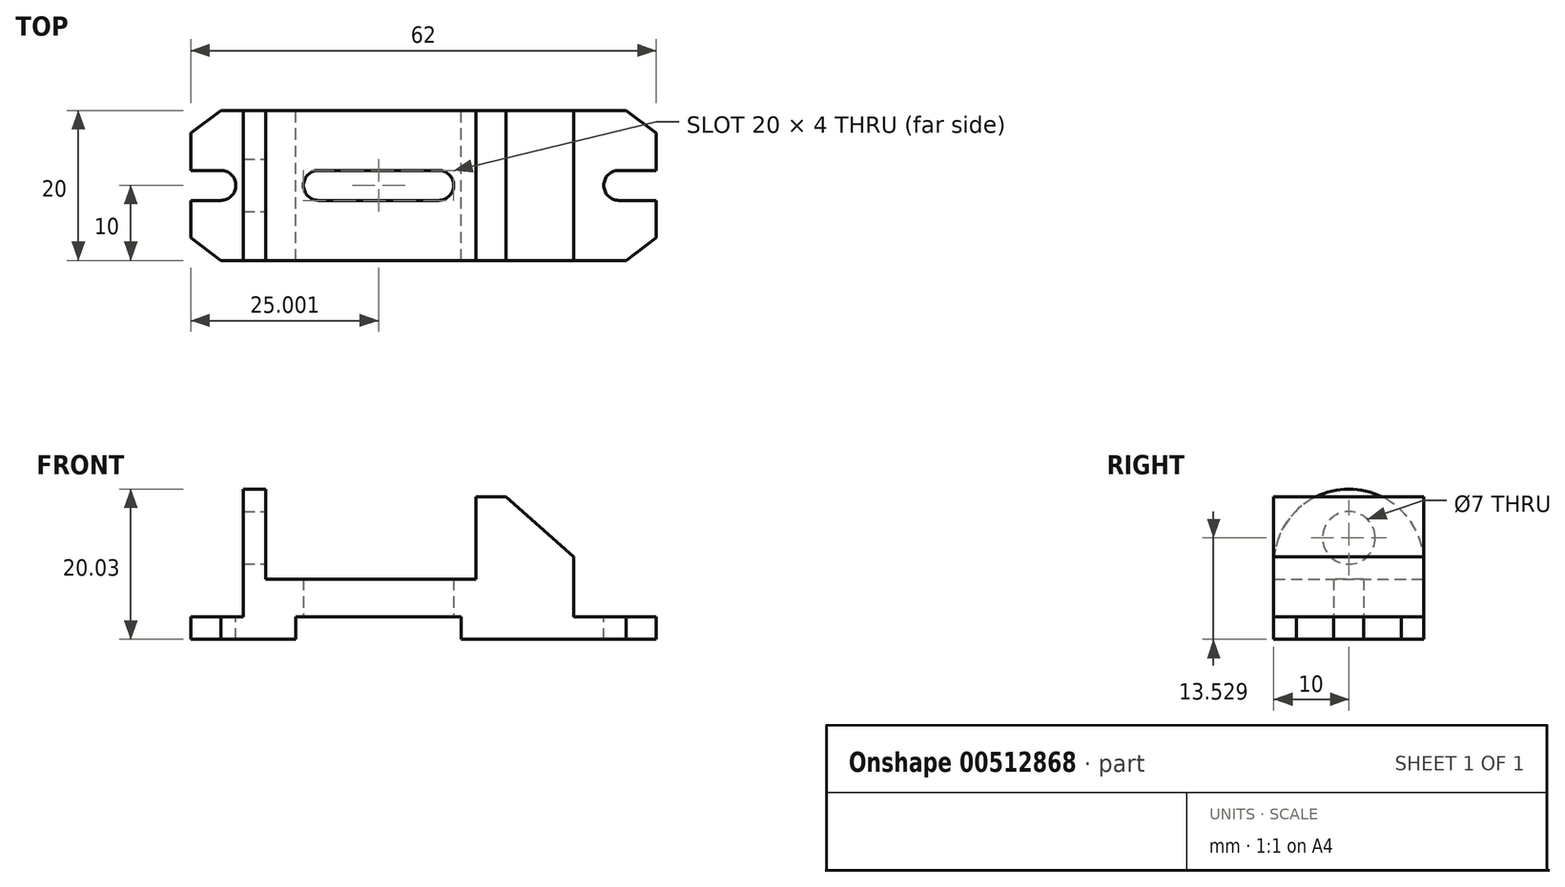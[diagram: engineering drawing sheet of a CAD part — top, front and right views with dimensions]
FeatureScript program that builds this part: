
annotation { "Feature Type Name" : "Feature", "Feature Type Description" : "" }
export const myFeature = defineFeature(function(context is Context, id is Id, definition is map)
    precondition{}
    {
        {
            var Q0;
            Q0=qCreatedBy(makeId("Front.planeOp"),FACE);
            var sketch = newSketch(context, id + "F0", { "sketchPlane" : qUnion([Q0])});
            skLineSegment(sketch, "E0", {"start": v(-17.84, 0) * mm, "end": v(-17.84, 3) * mm});
            skLineSegment(sketch, "E1", {"start": v(-17.84, 3) * mm, "end": v(-14.84, 3) * mm});
            skLineSegment(sketch, "E2", {"start": v(-14.84, 3) * mm, "end": v(-14.84, 10.03) * mm});
            skLineSegment(sketch, "E3", {"start": v(-14.84, 10.03) * mm, "end": v(-11.84, 10.03) * mm});
            skLineSegment(sketch, "E4", {"start": v(-11.84, 10.03) * mm, "end": v(-11.84, 8.03) * mm});
            skLineSegment(sketch, "E5", {"start": v(-11.84, 8.03) * mm, "end": v(16.16, 8.03) * mm});
            skLineSegment(sketch, "E6", {"start": v(16.16, 8.03) * mm, "end": v(16.16, 19.03) * mm});
            skLineSegment(sketch, "E7", {"start": v(16.16, 19.03) * mm, "end": v(20.16, 19.03) * mm});
            skLineSegment(sketch, "E8", {"start": v(-17.84, 0) * mm, "end": v(-7.84, 0) * mm});
            skLineSegment(sketch, "E9", {"start": v(-7.84, 0) * mm, "end": v(-7.84, 3) * mm});
            skLineSegment(sketch, "E10", {"start": v(-7.84, 3) * mm, "end": v(14.16, 3) * mm});
            skLineSegment(sketch, "E11", {"start": v(14.16, 3) * mm, "end": v(14.16, 0) * mm});
            skLineSegment(sketch, "E12", {"start": v(14.16, 0) * mm, "end": v(36.16, 0) * mm});
            skLineSegment(sketch, "E13", {"start": v(36.16, 0) * mm, "end": v(36.16, 3) * mm});
            skLineSegment(sketch, "E14", {"start": v(36.16, 3) * mm, "end": v(29.16, 3) * mm});
            skLineSegment(sketch, "E15", {"start": v(29.16, 3) * mm, "end": v(29.16, 11) * mm});
            skLineSegment(sketch, "E16", {"start": v(20.16, 19.03) * mm, "end": v(29.16, 11) * mm});
            skSolve(sketch);
        }
        {
            var Q0;
            Q0 = qSketchRegion(id + "F0", true);
            extrude(context, id + "F1", {"entities" : qUnion([Q0]), "endBound" : BoundingType.SYMMETRIC, "depth" : 20 * mm, "offsetDistance" : 25 * mm});
        }
        {
            var Q0;
            Q0=makeQuery(id+"F1.opExtrude","SWEPT_FACE",FACE,{"disambiguationData":[OSD([sQuery(id+"F0.wireOp",EDGE,"E4")])]});
            var sketch = newSketch(context, id + "F2", { "sketchPlane" : qUnion([Q0])});
            skArc(sketch, "E17", {"start": v(10, 10.03) * mm, "mid": v(0, 20.03) * mm, "end": v(-10, 10.03) * mm});
            skSolve(sketch);
        }
        {
            var Q0;
            Q0=makeQuery(id+"F1.opExtrude","SWEPT_FACE",FACE,{"disambiguationData":[OSD([sQuery(id+"F0.wireOp",EDGE,"E14")])]});
            var sketch = newSketch(context, id + "F3", { "sketchPlane" : qUnion([Q0])});
            skLineSegment(sketch, "E18.bottom", {"start": v(36.16, 10) * mm, "end": v(40.16, 10) * mm});
            skLineSegment(sketch, "E18.top", {"start": v(36.16, -10) * mm, "end": v(40.16, -10) * mm});
            skLineSegment(sketch, "E18.left", {"start": v(36.16, 10) * mm, "end": v(36.16, -10) * mm});
            skLineSegment(sketch, "E18.right", {"start": v(40.16, 10) * mm, "end": v(40.16, -10) * mm});
            skLineSegment(sketch, "E19", {"start": v(40.16, 2) * mm, "end": v(35.16, 2) * mm});
            skLineSegment(sketch, "E20", {"start": v(40.16, -2) * mm, "end": v(35.16, -2) * mm});
            skArc(sketch, "E21", {"start": v(35.16, 2) * mm, "mid": v(33.16, 0) * mm, "end": v(35.16, -2) * mm});
            skLineSegment(sketch, "E22", {"start": v(40.16, -2) * mm, "end": v(40.16, -7) * mm});
            skLineSegment(sketch, "E23", {"start": v(40.16, 2) * mm, "end": v(40.16, 7) * mm});
            skLineSegment(sketch, "E24", {"start": v(36.16, -10) * mm, "end": v(40.16, -7) * mm});
            skLineSegment(sketch, "E25", {"start": v(36.16, 10) * mm, "end": v(40.16, 7) * mm});
            skSolve(sketch);
        }
        {
            var Q0;
            Q0 = qSketchRegion(id + "F3", true);
            extrude(context, id + "F4", {"entities" : qUnion([Q0]), "operationType" : NewBodyOperationType.ADD, "oppositeDirection" : true, "depth" : 3 * mm, "offsetDistance" : 25 * mm});
        }
        {
            var Q0;
            {var subQ0=sQuery(id+"F3.wireOp",EDGE,"E20");var subQ1=sQuery(id+"F3.wireOp",EDGE,"E18.left");var subQ2=makeQuery(id+"F3.imprint","INTERSECT",VERTEX,{"derivedFrom":[subQ1,subQ0]});Q0=makeQuery(id+"F3.imprint","IMPRINT",FACE,{"disambiguationData":[TD([[makeQuery(id+"F3.imprint","IMPRINT",EDGE,{"disambiguationData":[TD([[subQ2,-1.0]])],"derivedFrom":subQ1}),-1.0]])]});}
            var Q1;
            {var subQ5=sQuery(id+"F3.wireOp",EDGE,"E21");Q1=makeQuery(id+"F3.imprint","IMPRINT",FACE,{"disambiguationData":[TD([[makeQuery(id+"F3.imprint","IMPRINT",EDGE,{"derivedFrom":subQ5}),1.0]])]});}
            var Q2;
            {var subQ0=sQuery(id+"F3.wireOp",EDGE,"E18.top");Q2=makeQuery(id+"F3.imprint","IMPRINT",FACE,{"disambiguationData":[TD([[makeQuery(id+"F3.imprint","IMPRINT",EDGE,{"derivedFrom":subQ0}),1.0]])]});}
            var Q3;
            {var subQ0=sQuery(id+"F3.wireOp",EDGE,"E18.bottom");Q3=makeQuery(id+"F3.imprint","IMPRINT",FACE,{"disambiguationData":[TD([[makeQuery(id+"F3.imprint","IMPRINT",EDGE,{"derivedFrom":subQ0}),-1.0]])]});}
            extrude(context, id + "F5", {"entities" : qUnion([Q0, Q1, Q2, Q3]), "operationType" : NewBodyOperationType.REMOVE, "oppositeDirection" : true, "depth" : 3 * mm, "offsetDistance" : 25 * mm});
        }
        {
            var Q0;
            Q0=makeQuery(id+"F1.opExtrude","SWEPT_FACE",FACE,{"disambiguationData":[OSD([sQuery(id+"F0.wireOp",EDGE,"E1")])]});
            var sketch = newSketch(context, id + "F6", { "sketchPlane" : qUnion([Q0])});
            skLineSegment(sketch, "E26.left", {"start": v(-17.84, 10) * mm, "end": v(-17.84, -10) * mm});
            skLineSegment(sketch, "E26.right", {"start": v(-21.84, 7) * mm, "end": v(-21.84, 2) * mm});
            skLineSegment(sketch, "E27", {"start": v(-17.84, -2) * mm, "end": v(-21.84, -2) * mm});
            skLineSegment(sketch, "E28", {"start": v(-17.84, 2) * mm, "end": v(-21.84, 2) * mm});
            skArc(sketch, "E29", {"start": v(-17.84, -2) * mm, "mid": v(-15.84, 0) * mm, "end": v(-17.84, 2) * mm});
            skLineSegment(sketch, "E30", {"start": v(-21.84, 2) * mm, "end": v(-21.84, 7) * mm});
            skLineSegment(sketch, "E31", {"start": v(-21.84, -2) * mm, "end": v(-21.84, -7) * mm});
            skLineSegment(sketch, "E32", {"start": v(-17.84, 10) * mm, "end": v(-21.84, 7) * mm});
            skLineSegment(sketch, "E33", {"start": v(-17.84, -10) * mm, "end": v(-21.84, -7) * mm});
            skPoint(sketch, "E26.top.end.orphan", {"position": v(-21.84, -10) * mm});
            skSolve(sketch);
        }
        {
            var Q0;
            {var subQ2=sQuery(id+"F6.wireOp",EDGE,"E28");Q0=makeQuery(id+"F6.imprint","IMPRINT",FACE,{"disambiguationData":[TD([[makeQuery(id+"F6.imprint","IMPRINT",EDGE,{"derivedFrom":subQ2}),-1.0]])]});}
            var Q1;
            {var subQ2=sQuery(id+"F6.wireOp",EDGE,"E27");Q1=makeQuery(id+"F6.imprint","IMPRINT",FACE,{"disambiguationData":[TD([[makeQuery(id+"F6.imprint","IMPRINT",EDGE,{"derivedFrom":subQ2}),1.0]])]});}
            extrude(context, id + "F7", {"entities" : qUnion([Q0, Q1]), "operationType" : NewBodyOperationType.ADD, "oppositeDirection" : true, "depth" : 3 * mm, "offsetDistance" : 25 * mm});
        }
        {
            var Q0;
            {var subQ0=sQuery(id+"F6.wireOp",EDGE,"E29");Q0=makeQuery(id+"F6.imprint","IMPRINT",FACE,{"disambiguationData":[TD([[makeQuery(id+"F6.imprint","IMPRINT",EDGE,{"derivedFrom":subQ0}),1.0]])]});}
            extrude(context, id + "F8", {"entities" : qUnion([Q0]), "operationType" : NewBodyOperationType.REMOVE, "oppositeDirection" : true, "depth" : 3 * mm, "offsetDistance" : 25 * mm});
        }
        {
            var Q0;
            Q0=makeQuery(id+"F1.opExtrude","SWEPT_FACE",FACE,{"disambiguationData":[OSD([sQuery(id+"F0.wireOp",EDGE,"E10")])]});
            var sketch = newSketch(context, id + "F9", { "sketchPlane" : qUnion([Q0])});
            skLineSegment(sketch, "E34.bottom", {"start": v(-4.84, 2) * mm, "end": v(11.16, 2) * mm});
            skLineSegment(sketch, "E34.top", {"start": v(-4.84, -2) * mm, "end": v(11.16, -2) * mm});
            skLineSegment(sketch, "E34.left", {"start": v(-4.84, 2) * mm, "end": v(-4.84, -2) * mm});
            skLineSegment(sketch, "E34.right", {"start": v(11.16, 2) * mm, "end": v(11.16, -2) * mm});
            skLineSegment(sketch, "E35.0", {"start": v(-17.84, 2) * mm, "end": v(-21.84, 2) * mm});
            skLineSegment(sketch, "E36.0", {"start": v(-17.84, -2) * mm, "end": v(-21.84, -2) * mm});
            skLineSegment(sketch, "E37.0", {"start": v(-17.84, 10) * mm, "end": v(-7.84, 10) * mm});
            skArc(sketch, "E38", {"start": v(-4.84, 2) * mm, "mid": v(-6.84, 0) * mm, "end": v(-4.84, -2) * mm});
            skArc(sketch, "E39", {"start": v(11.16, -2) * mm, "mid": v(13.16, 0) * mm, "end": v(11.16, 2) * mm});
            skSolve(sketch);
        }
        {
            var Q0;
            Q0 = qSketchRegion(id + "F9", true);
            extrude(context, id + "F10", {"entities" : qUnion([Q0]), "operationType" : NewBodyOperationType.REMOVE, "oppositeDirection" : true, "depth" : 6 * mm, "offsetDistance" : 25 * mm});
        }
        {
            var Q0;
            Q0=makeQuery(id+"F2.imprint","IMPRINT",FACE,{"disambiguationData":[TD([[makeQuery(id+"F2.imprint","IMPRINT",EDGE,{"derivedFrom":sQuery(id+"F2.wireOp",EDGE,"E17")}),1.0]])]});
            extrude(context, id + "F11", {"entities" : qUnion([Q0]), "operationType" : NewBodyOperationType.ADD, "oppositeDirection" : true, "depth" : 3 * mm, "offsetDistance" : 25 * mm});
        }
        {
            var Q0;
            Q0=makeQuery(id+"F2.imprint","IMPRINT",FACE,{"disambiguationData":[TD([[makeQuery(id+"F2.imprint","IMPRINT",EDGE,{"derivedFrom":sQuery(id+"F2.wireOp",EDGE,"E17")}),1.0]])]});
            var sketch = newSketch(context, id + "F12", { "sketchPlane" : qUnion([Q0])});
            skCircle(sketch, "E40", {"center": v(0, 13.53) * mm, "radius": 3.5 * mm});
            skSolve(sketch);
        }
        {
            var Q0;
            Q0 = qSketchRegion(id + "F12", true);
            extrude(context, id + "F13", {"entities" : qUnion([Q0]), "operationType" : NewBodyOperationType.REMOVE, "oppositeDirection" : true, "depth" : 3 * mm, "offsetDistance" : 25 * mm});
        }
    });
